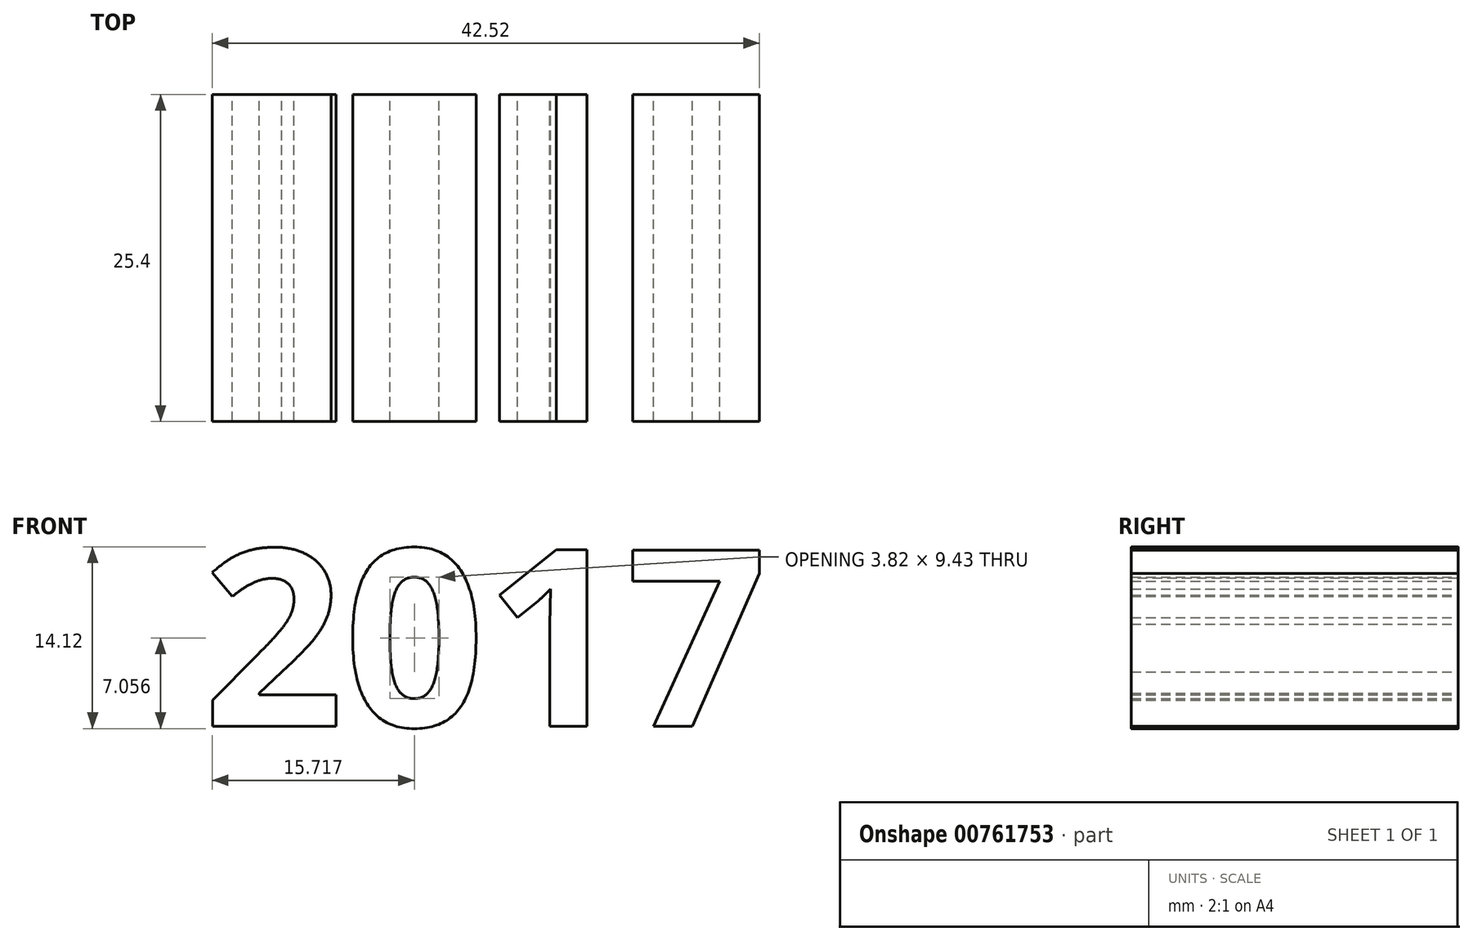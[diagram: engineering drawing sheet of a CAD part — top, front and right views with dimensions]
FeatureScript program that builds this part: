
annotation { "Feature Type Name" : "Feature", "Feature Type Description" : "" }
export const myFeature = defineFeature(function(context is Context, id is Id, definition is map)
    precondition{}
    {
        {
            var Q0;
            Q0=qCreatedBy(makeId("Front.planeOp"),FACE);
            var sketch = newSketch(context, id + "F0", { "sketchPlane" : qUnion([Q0])});
            skText(sketch, "E0", { "text": "2017", "fontName": "OpenSans-Bold.ttf"});
            const initialGuessF0  = {"E0": [-0.04448, 0, 1, 0, 0.01383]};
            skSetInitialGuess(sketch, initialGuessF0);
            skSolve(sketch);
        }
        {
            var Q0;
            Q0 = qSketchRegion(id + "F0", true);
            extrude(context, id + "F1", {"entities" : qUnion([Q0]), "depth" : 25.4 * mm, "offsetDistance" : 25.4 * mm});
        }
    });
